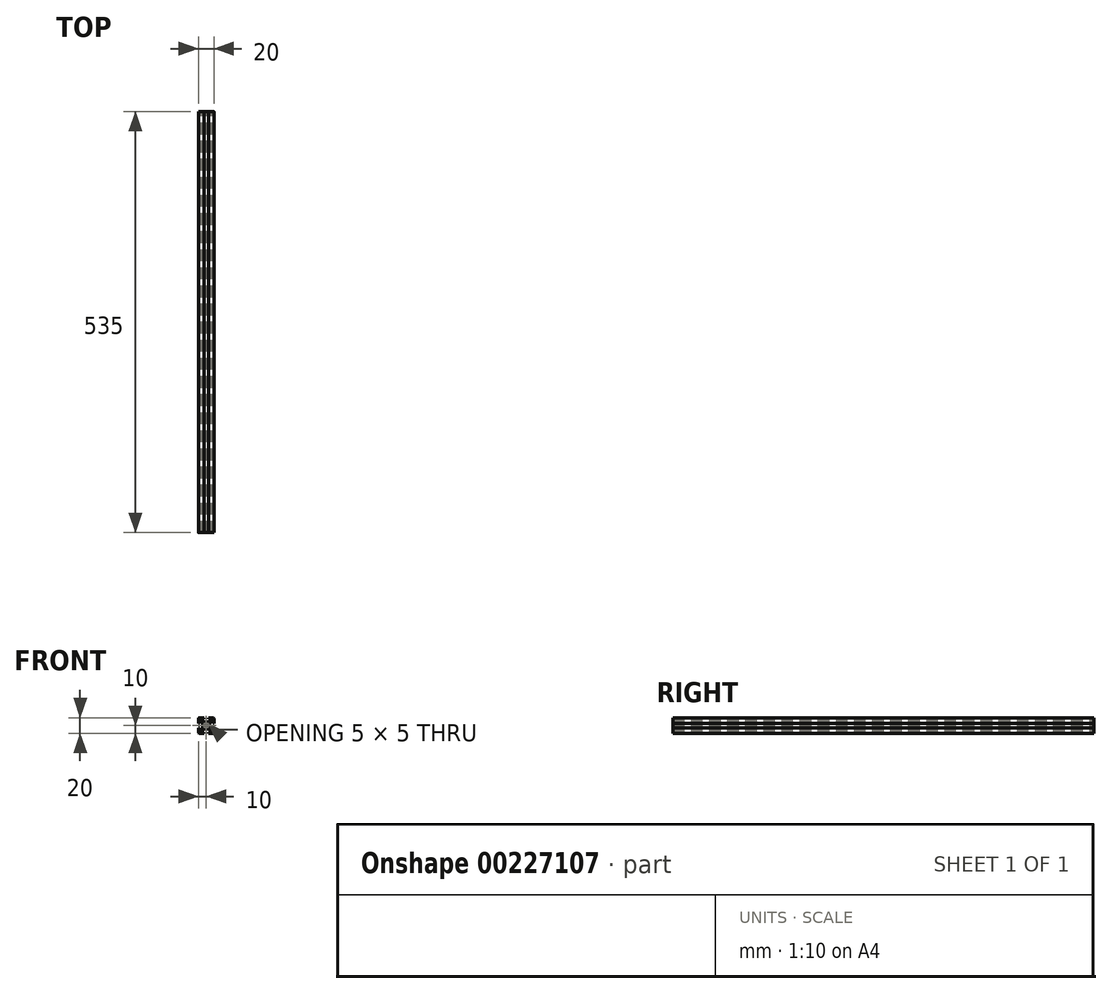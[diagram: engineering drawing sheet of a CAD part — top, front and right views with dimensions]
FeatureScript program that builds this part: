
annotation { "Feature Type Name" : "Feature", "Feature Type Description" : "" }
export const myFeature = defineFeature(function(context is Context, id is Id, definition is map)
    precondition{}
    {
        {
            var Q0;
            Q0=qCreatedBy(makeId("Front.planeOp"),FACE);
            var sketch = newSketch(context, id + "F0", { "sketchPlane" : qUnion([Q0])});
            skLineSegment(sketch, "E0.bottom", {"start": v(8.5, -10) * mm, "end": v(3, -10) * mm});
            skLineSegment(sketch, "E0.top", {"start": v(8.5, 10) * mm, "end": v(3, 10) * mm});
            skLineSegment(sketch, "E0.left", {"start": v(10, -8.5) * mm, "end": v(10, -3) * mm});
            skLineSegment(sketch, "E0.right", {"start": v(-10, -8.5) * mm, "end": v(-10, -3) * mm});
            skPoint(sketch, "E0.middle", {"position": v(0, 0) * mm});
            skLineSegment(sketch, "E1.bottom", {"start": v(6, -8.5) * mm, "end": v(3, -8.5) * mm});
            skLineSegment(sketch, "E1.top", {"start": v(6, 8.5) * mm, "end": v(3, 8.5) * mm});
            skLineSegment(sketch, "E1.left", {"start": v(8.5, -6) * mm, "end": v(8.5, -3) * mm});
            skLineSegment(sketch, "E1.right", {"start": v(-8.5, -6) * mm, "end": v(-8.5, -3) * mm});
            skLineSegment(sketch, "E2.bottom", {"start": v(3.44, -4.5) * mm, "end": v(-3.44, -4.5) * mm});
            skLineSegment(sketch, "E2.top", {"start": v(3.44, 4.5) * mm, "end": v(-3.44, 4.5) * mm});
            skLineSegment(sketch, "E2.left", {"start": v(4.5, -3.44) * mm, "end": v(4.5, 3.44) * mm});
            skLineSegment(sketch, "E2.right", {"start": v(-4.5, -3.44) * mm, "end": v(-4.5, 3.44) * mm});
            skLineSegment(sketch, "E3.bottom", {"start": v(8.5, -6) * mm, "end": v(7.06, -6) * mm});
            skLineSegment(sketch, "E3.top", {"start": v(8.5, 6) * mm, "end": v(7.06, 6) * mm});
            skLineSegment(sketch, "E4.left", {"start": v(6, -8.5) * mm, "end": v(6, -7.06) * mm});
            skLineSegment(sketch, "E4.right", {"start": v(-6, -8.5) * mm, "end": v(-6, -7.06) * mm});
            skPoint(sketch, "E5.orphan", {"position": v(-8.5, 8.5) * mm});
            skPoint(sketch, "E6.orphan", {"position": v(8.5, 8.5) * mm});
            skPoint(sketch, "E7.orphan", {"position": v(8.5, -8.5) * mm});
            skPoint(sketch, "E8.orphan", {"position": v(-8.5, -8.5) * mm});
            skLineSegment(sketch, "E9.trimOffspring", {"start": v(-6, 7.06) * mm, "end": v(-6, 8.5) * mm});
            skLineSegment(sketch, "E10.trimOffspring", {"start": v(-7.06, 6) * mm, "end": v(-8.5, 6) * mm});
            skLineSegment(sketch, "E11.trimOffspring", {"start": v(6, 7.06) * mm, "end": v(6, 8.5) * mm});
            skLineSegment(sketch, "E12.trimOffspring", {"start": v(-7.06, -6) * mm, "end": v(-8.5, -6) * mm});
            skLineSegment(sketch, "E13", {"start": v(-10, 10) * mm, "end": v(0, 0) * mm, "construction": true});
            skLineSegment(sketch, "E14", {"start": v(10, 10) * mm, "end": v(0, 0) * mm, "construction": true});
            skLineSegment(sketch, "E15", {"start": v(-6, 7.06) * mm, "end": v(-3.44, 4.5) * mm});
            skPoint(sketch, "E15.endSnap0", {"position": v(7.25, -6) * mm});
            skLineSegment(sketch, "E16", {"start": v(6, -7.06) * mm, "end": v(3.44, -4.5) * mm});
            skLineSegment(sketch, "E17", {"start": v(7.06, 6) * mm, "end": v(4.5, 3.44) * mm});
            skLineSegment(sketch, "E18", {"start": v(6, 7.06) * mm, "end": v(3.44, 4.5) * mm});
            skPoint(sketch, "E19.orphan", {"position": v(6, -6) * mm});
            skPoint(sketch, "E20.orphan", {"position": v(-4.5, -4.5) * mm});
            skPoint(sketch, "E21.orphan", {"position": v(-4.5, 4.5) * mm});
            skPoint(sketch, "E22.orphan", {"position": v(4.5, 4.5) * mm});
            skPoint(sketch, "E23.orphan", {"position": v(4.5, -4.5) * mm});
            skLineSegment(sketch, "E24.trimOffspring", {"start": v(4.5, -3.44) * mm, "end": v(7.06, -6) * mm});
            skLineSegment(sketch, "E25.trimOffspring", {"start": v(-3.44, -4.5) * mm, "end": v(-6, -7.06) * mm});
            skLineSegment(sketch, "E26.trimOffspring", {"start": v(-4.5, -3.44) * mm, "end": v(-7.06, -6) * mm});
            skLineSegment(sketch, "E27.trimOffspring", {"start": v(-4.5, 3.44) * mm, "end": v(-7.06, 6) * mm});
            skLineSegment(sketch, "E28.bottom", {"start": v(8.5, -3) * mm, "end": v(10, -3) * mm});
            skLineSegment(sketch, "E28.top", {"start": v(8.5, 3) * mm, "end": v(10, 3) * mm});
            skPoint(sketch, "E28.middle", {"position": v(10, 0) * mm});
            skLineSegment(sketch, "E29.left", {"start": v(3, 8.5) * mm, "end": v(3, 10) * mm});
            skLineSegment(sketch, "E29.right", {"start": v(-3, 8.5) * mm, "end": v(-3, 10) * mm});
            skPoint(sketch, "E29.middle", {"position": v(0, 10) * mm});
            skLineSegment(sketch, "E30.bottom", {"start": v(-8.5, 3) * mm, "end": v(-10, 3) * mm});
            skLineSegment(sketch, "E30.top", {"start": v(-8.5, -3) * mm, "end": v(-10, -3) * mm});
            skPoint(sketch, "E30.middle", {"position": v(-10, 0) * mm});
            skLineSegment(sketch, "E31.left", {"start": v(3, -8.5) * mm, "end": v(3, -10) * mm});
            skLineSegment(sketch, "E31.right", {"start": v(-3, -8.5) * mm, "end": v(-3, -10) * mm});
            skPoint(sketch, "E31.middle", {"position": v(0, -10) * mm});
            skPoint(sketch, "E32.orphan", {"position": v(3, 11.5) * mm});
            skPoint(sketch, "E33.orphan", {"position": v(-3, 11.5) * mm});
            skLineSegment(sketch, "E34.trimOffspring", {"start": v(-3, 10) * mm, "end": v(-8.5, 10) * mm});
            skLineSegment(sketch, "E35.trimOffspring", {"start": v(-3, 8.5) * mm, "end": v(-6, 8.5) * mm});
            skPoint(sketch, "E28.right.end.orphan", {"position": v(11.5, 3) * mm});
            skPoint(sketch, "E36.orphan", {"position": v(11.5, -3) * mm});
            skLineSegment(sketch, "E37.trimOffspring", {"start": v(10, 3) * mm, "end": v(10, 8.5) * mm});
            skLineSegment(sketch, "E38.trimOffspring", {"start": v(8.5, 3) * mm, "end": v(8.5, 6) * mm});
            skPoint(sketch, "E39.orphan", {"position": v(3, -11.5) * mm});
            skPoint(sketch, "E40.orphan", {"position": v(-3, -11.5) * mm});
            skLineSegment(sketch, "E41.trimOffspring", {"start": v(-3, -10) * mm, "end": v(-8.5, -10) * mm});
            skLineSegment(sketch, "E42.trimOffspring", {"start": v(-3, -8.5) * mm, "end": v(-6, -8.5) * mm});
            skPoint(sketch, "E30.right.end.orphan", {"position": v(-11.5, -3) * mm});
            skPoint(sketch, "E43.orphan", {"position": v(-11.5, 3) * mm});
            skLineSegment(sketch, "E44.trimOffspring", {"start": v(-10, 3) * mm, "end": v(-10, 8.5) * mm});
            skLineSegment(sketch, "E45.trimOffspring", {"start": v(-8.5, 3) * mm, "end": v(-8.5, 6) * mm});
            skLineSegment(sketch, "E46.trimOffspring", {"start": v(0, 0) * mm, "end": v(10, -10) * mm, "construction": true});
            skLineSegment(sketch, "E47.trimOffspring", {"start": v(0, 0) * mm, "end": v(-10, -10) * mm, "construction": true});
            skArc(sketch, "E48", {"start": v(1.16, 2.22) * mm, "mid": v(0, 2.5) * mm, "end": v(-1.16, 2.22) * mm});
            skLineSegment(sketch, "E49", {"start": v(-2.5, -1.44) * mm, "end": v(1.44, 2.5) * mm});
            skLineSegment(sketch, "E50", {"start": v(2.5, 1.44) * mm, "end": v(-1.44, -2.5) * mm});
            skLineSegment(sketch, "E51", {"start": v(1.44, -2.5) * mm, "end": v(-2.5, 1.44) * mm});
            skLineSegment(sketch, "E52", {"start": v(-1.44, 2.5) * mm, "end": v(2.5, -1.44) * mm});
            skLineSegment(sketch, "E53", {"start": v(2.5, 1.44) * mm, "end": v(2.5, -1.44) * mm, "construction": true});
            skLineSegment(sketch, "E54", {"start": v(1.44, -2.5) * mm, "end": v(-1.44, -2.5) * mm, "construction": true});
            skLineSegment(sketch, "E55", {"start": v(-2.5, -1.44) * mm, "end": v(-2.5, 1.44) * mm, "construction": true});
            skLineSegment(sketch, "E56", {"start": v(-1.44, 2.5) * mm, "end": v(1.44, 2.5) * mm, "construction": true});
            skLineSegment(sketch, "E57", {"start": v(-1.44, 2.5) * mm, "end": v(-2.5, 1.44) * mm});
            skLineSegment(sketch, "E58", {"start": v(1.44, 2.5) * mm, "end": v(2.5, 1.44) * mm});
            skLineSegment(sketch, "E59", {"start": v(2.5, -1.44) * mm, "end": v(1.44, -2.5) * mm});
            skLineSegment(sketch, "E60", {"start": v(-1.44, -2.5) * mm, "end": v(-2.5, -1.44) * mm});
            skArc(sketch, "E61.trimOffspring", {"start": v(-2.22, 1.16) * mm, "mid": v(-2.5, 0) * mm, "end": v(-2.22, -1.16) * mm});
            skArc(sketch, "E62.trimOffspring", {"start": v(-1.16, -2.22) * mm, "mid": v(0, -2.5) * mm, "end": v(1.16, -2.22) * mm});
            skArc(sketch, "E63.trimOffspring", {"start": v(2.22, -1.16) * mm, "mid": v(2.5, 0) * mm, "end": v(2.22, 1.16) * mm});
            skPoint(sketch, "E64.visualSharp", {"position": v(10, 10) * mm});
            skArc(sketch, "E64.filletArc", {"start": v(10, 8.5) * mm, "mid": v(9.56, 9.56) * mm, "end": v(8.5, 10) * mm});
            skPoint(sketch, "E65.visualSharp", {"position": v(10, -10) * mm});
            skArc(sketch, "E65.filletArc", {"start": v(8.5, -10) * mm, "mid": v(9.56, -9.56) * mm, "end": v(10, -8.5) * mm});
            skPoint(sketch, "E66.visualSharp", {"position": v(-10, -10) * mm});
            skArc(sketch, "E66.filletArc", {"start": v(-10, -8.5) * mm, "mid": v(-9.56, -9.56) * mm, "end": v(-8.5, -10) * mm});
            skPoint(sketch, "E67.visualSharp", {"position": v(-10, 10) * mm});
            skArc(sketch, "E67.filletArc", {"start": v(-8.5, 10) * mm, "mid": v(-9.56, 9.56) * mm, "end": v(-10, 8.5) * mm});
            skSolve(sketch);
        }
        {
            assignVariable(context, id + "F2", {"name" : "Length", "anyValue" : 535});
        }
        {
            var Q0;
            Q0=qSketchRegion(id+"F0",true);
            extrude(context, id + "F1", {"entities" : qUnion([Q0]), "depth" : (getVariable(context, 'Length')) * mm});
        }
    });
